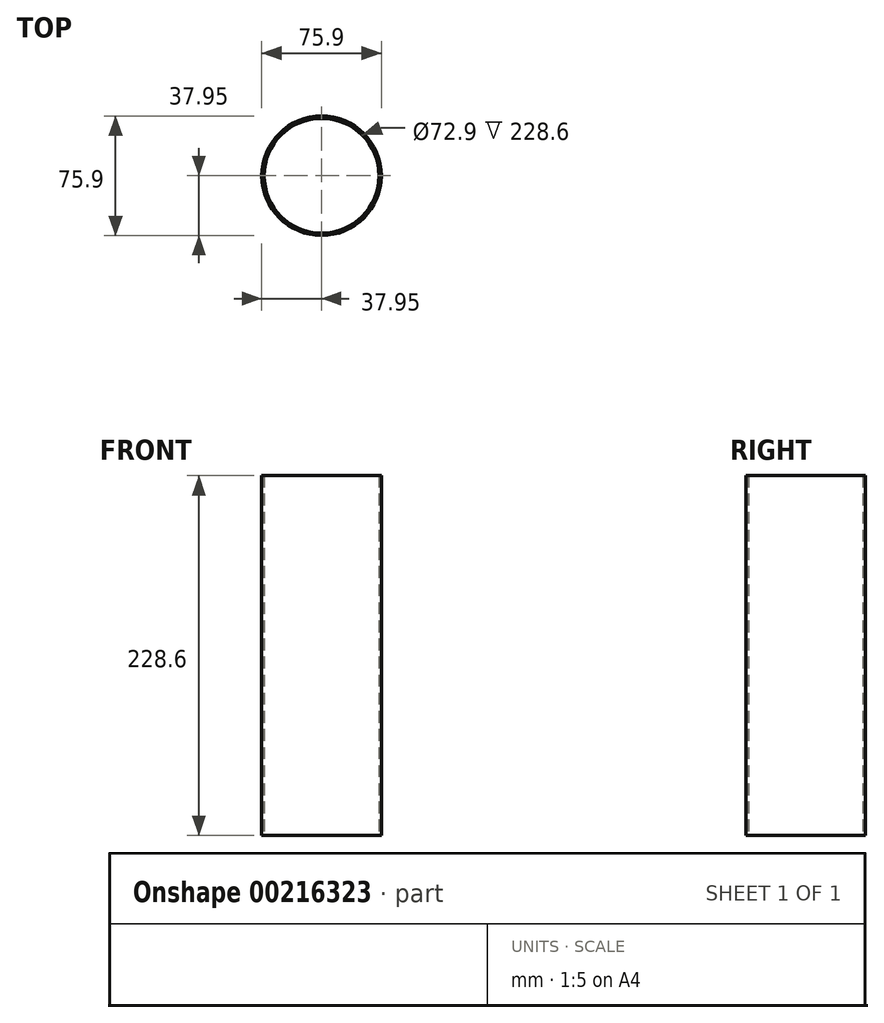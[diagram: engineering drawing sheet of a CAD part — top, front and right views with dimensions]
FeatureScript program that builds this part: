
annotation { "Feature Type Name" : "Feature", "Feature Type Description" : "" }
export const myFeature = defineFeature(function(context is Context, id is Id, definition is map)
    precondition{}
    {
        {
            var Q0;
            Q0=qCreatedBy(makeId("Top.planeOp"),FACE);
            var sketch = newSketch(context, id + "F0", { "sketchPlane" : qUnion([Q0])});
            skCircle(sketch, "E0", {"center": v(0, 0) * mm, "radius": 37.95 * mm});
            skCircle(sketch, "E1", {"center": v(0, 0) * mm, "radius": 36.45 * mm});
            skSolve(sketch);
        }
        {
            var Q0;
            Q0 = qSketchRegion(id + "F0", true);
            extrude(context, id + "F1", {"entities" : qUnion([Q0]), "depth" : 228.6 * mm});
        }
    });
